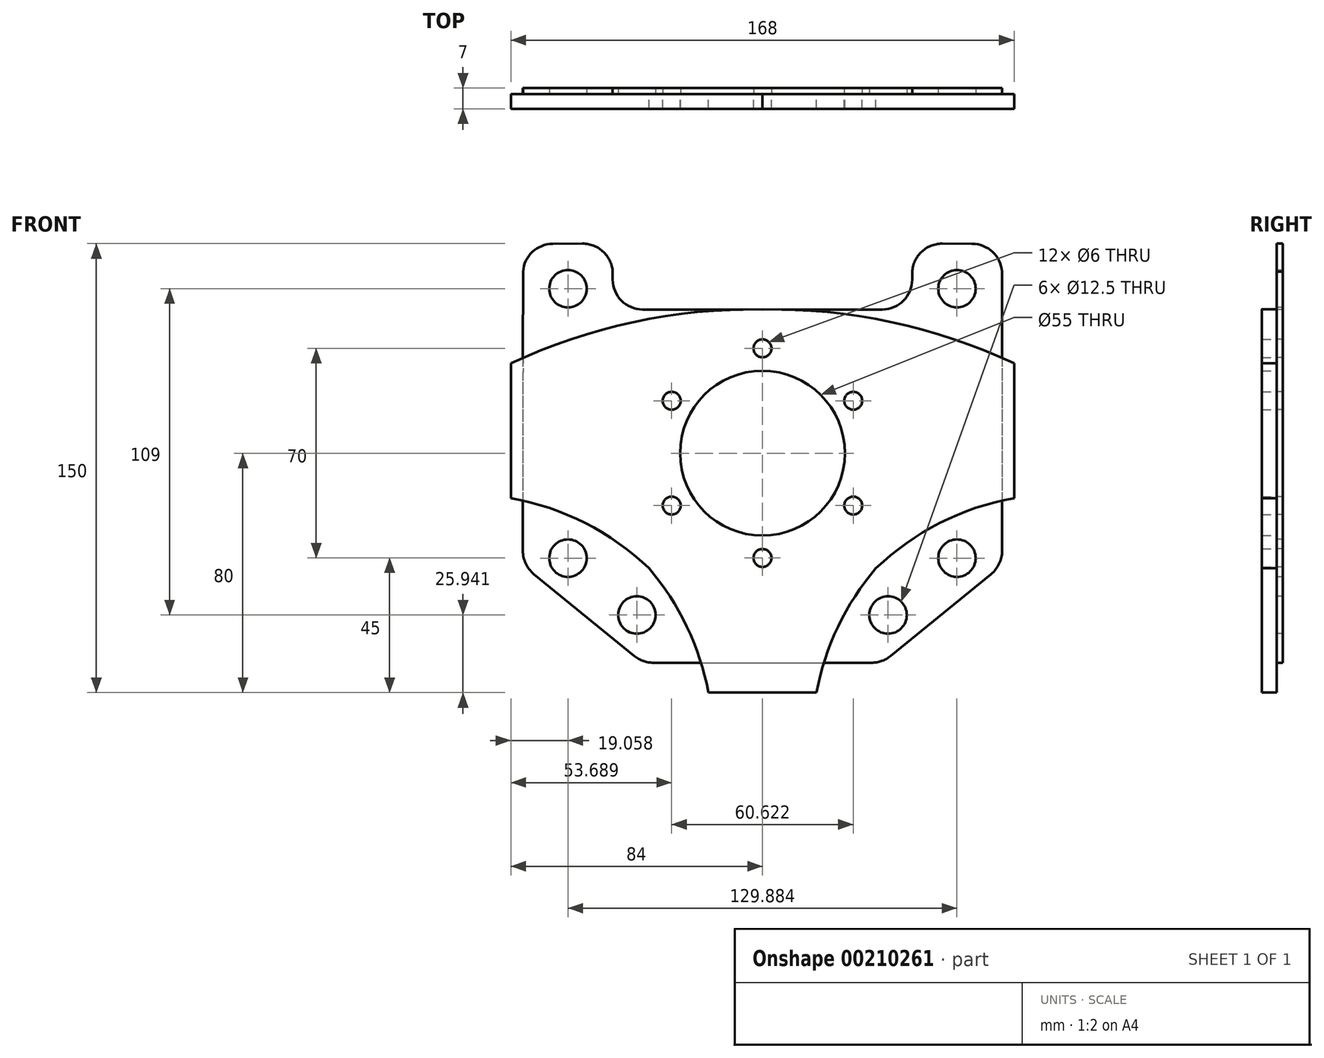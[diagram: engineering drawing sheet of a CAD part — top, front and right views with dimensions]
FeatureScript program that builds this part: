
annotation { "Feature Type Name" : "Feature", "Feature Type Description" : "" }
export const myFeature = defineFeature(function(context is Context, id is Id, definition is map)
    precondition{}
    {
        {
            var Q0;
            Q0=qCreatedBy(makeId("Front.planeOp"),FACE);
            var sketch = newSketch(context, id + "F0", { "sketchPlane" : qUnion([Q0])});
            skCircle(sketch, "E0", {"center": v(0, 0) * mm, "radius": 27.5 * mm});
            skCircle(sketch, "E1", {"center": v(0, 35) * mm, "radius": 3 * mm});
            skCircle(sketch, "E2.1.0", {"center": v(-30.31, 17.5) * mm, "radius": 3 * mm});
            skCircle(sketch, "E2.2.0", {"center": v(-30.31, -17.5) * mm, "radius": 3 * mm});
            skCircle(sketch, "E2.3.0", {"center": v(0, -35) * mm, "radius": 3 * mm});
            skCircle(sketch, "E2.4.0", {"center": v(30.31, -17.5) * mm, "radius": 3 * mm});
            skCircle(sketch, "E2.5.0", {"center": v(30.31, 17.5) * mm, "radius": 3 * mm});
            skLineSegment(sketch, "E3", {"start": v(0, -80) * mm, "end": v(-18, -80) * mm});
            skArc(sketch, "E4", {"start": v(-37.9, -38.47) * mm, "mid": v(-59.22, -23.35) * mm, "end": v(-84, -15) * mm});
            skArc(sketch, "E5", {"start": v(-18, -80) * mm, "mid": v(-25.25, -57.94) * mm, "end": v(-37.9, -38.47) * mm});
            skLineSegment(sketch, "E6", {"start": v(-84, 30) * mm, "end": v(-84, -15) * mm});
            skArc(sketch, "E7", {"start": v(0, 48) * mm, "mid": v(-43.03, 43.8) * mm, "end": v(-84, 30) * mm});
            skArc(sketch, "E8.MirrorCS", {"start": v(0, 48) * mm, "mid": v(43.03, 43.8) * mm, "end": v(84, 30) * mm});
            skLineSegment(sketch, "E9.MirrorCS", {"start": v(84, 30) * mm, "end": v(84, -15) * mm});
            skLineSegment(sketch, "E10.MirrorCS", {"start": v(84, -15) * mm, "end": v(84, -15) * mm});
            skArc(sketch, "E11.MirrorCS", {"start": v(37.9, -38.47) * mm, "mid": v(59.22, -23.35) * mm, "end": v(84, -15) * mm});
            skArc(sketch, "E12.MirrorCS", {"start": v(18, -80) * mm, "mid": v(25.25, -57.94) * mm, "end": v(37.9, -38.47) * mm});
            skLineSegment(sketch, "E13.MirrorCS", {"start": v(0, -80) * mm, "end": v(18, -80) * mm});
            skLineSegment(sketch, "E14", {"start": v(0, 0) * mm, "end": v(37.9, -38.47) * mm});
            skSolve(sketch);
        }
        {
            var Q0;
            Q0=makeQuery(id+"F0.imprint","IMPRINT",FACE,{"disambiguationData":[TD([[makeQuery(id+"F0.imprint","IMPRINT",EDGE,{"derivedFrom":sQuery(id+"F0.wireOp",EDGE,"xvLfkQ3F-fgjy-q9Nn-lcfM-oA4vtxVeLGYN")}),-1.0]])]});
            var Q1;
            {var subQ0=sQuery(id+"F0.wireOp",EDGE,"IXeQJo4f-0NGN-wymH-wL35-tD5XUzaEt9Ii");Q1=makeQuery(id+"F0.imprint","IMPRINT",FACE,{"disambiguationData":[TD([[makeQuery(id+"F0.imprint","IMPRINT",EDGE,{"derivedFrom":subQ0}),-1.0]])]});}
            var Q2;
            Q2=makeQuery(id+"F0.imprint","IMPRINT",FACE,{"disambiguationData":[TD([[makeQuery(id+"F0.imprint","IMPRINT",EDGE,{"derivedFrom":sQuery(id+"F0.wireOp",EDGE,"E0")}),-1.0]])]});
            var Q3;
            {var subQ0=sQuery(id+"F0.wireOp",EDGE,"U97vX6Bn-T6Nm-C19i-UCoZ-bPOguSU8hI4x");Q3=makeQuery(id+"F0.imprint","IMPRINT",FACE,{"disambiguationData":[TD([[makeQuery(id+"F0.imprint","IMPRINT",EDGE,{"derivedFrom":subQ0}),-1.0]])]});}
            var Q4;
            Q4=makeQuery(id+"F0.imprint","IMPRINT",FACE,{"disambiguationData":[TD([[makeQuery(id+"F0.imprint","IMPRINT",EDGE,{"derivedFrom":sQuery(id+"F0.wireOp",EDGE,"iTDH6eJd-3ZuL-mUN2-QFPx-3khqCnK7DwfM")}),-1.0]])]});
            var Q5;
            {var subQ0=sQuery(id+"F0.wireOp",EDGE,"LSPlpz0O-uzcR-zpDg-bx14-Tm5pNzSKurLG");Q5=makeQuery(id+"F0.imprint","IMPRINT",FACE,{"disambiguationData":[TD([[makeQuery(id+"F0.imprint","IMPRINT",EDGE,{"derivedFrom":subQ0}),-1.0]])]});}
            var Q6;
            Q6=makeQuery(id+"F0.imprint","IMPRINT",FACE,{"disambiguationData":[TD([[makeQuery(id+"F0.imprint","IMPRINT",EDGE,{"derivedFrom":sQuery(id+"F0.wireOp",EDGE,"9da5268f-547f-4821-a759-cff2299c6b0c0.MirrorC")}),1.0]])]});
            var Q7;
            Q7=makeQuery(id+"F0.imprint","IMPRINT",FACE,{"disambiguationData":[TD([[makeQuery(id+"F0.imprint","IMPRINT",EDGE,{"derivedFrom":sQuery(id+"F0.wireOp",EDGE,"5ea91802-01c1-4fcd-b629-e54decbf77210.MirrorC")}),1.0]])]});
            extrude(context, id + "F1", {"entities" : qUnion([Q0, Q1, Q2, Q3, Q4, Q5, Q6, Q7]), "depth" : 5 * mm});
        }
        {
            var Q0;
            Q0=qCreatedBy(makeId("Front.planeOp"),FACE);
            var sketch = newSketch(context, id + "F2", { "sketchPlane" : qUnion([Q0])});
            skLineSegment(sketch, "E15", {"start": v(0, 48) * mm, "end": v(-40, 48) * mm});
            skLineSegment(sketch, "E16", {"start": v(-50, 58) * mm, "end": v(-50, 60) * mm});
            skLineSegment(sketch, "E17", {"start": v(-60.06, 70) * mm, "end": v(-70.02, 69.94) * mm});
            skPoint(sketch, "E18.visualSharp", {"position": v(-80.06, 69.88) * mm});
            skArc(sketch, "E18.filletArc", {"start": v(-70.02, 69.94) * mm, "mid": v(-76.81, 67.23) * mm, "end": v(-79.94, 60.62) * mm});
            skPoint(sketch, "E19.visualSharp", {"position": v(-50, 70.06) * mm});
            skArc(sketch, "E19.filletArc", {"start": v(-50, 60) * mm, "mid": v(-52.95, 67.1) * mm, "end": v(-60.06, 70) * mm});
            skPoint(sketch, "E20.visualSharp", {"position": v(-50, 48) * mm});
            skArc(sketch, "E20.filletArc", {"start": v(-50, 58) * mm, "mid": v(-47.07, 50.93) * mm, "end": v(-40, 48) * mm});
            skLineSegment(sketch, "E21", {"start": v(0, 0) * mm, "end": v(0, 35) * mm});
            skCircle(sketch, "E22", {"center": v(0, 35) * mm, "radius": 3 * mm});
            skLineSegment(sketch, "E23", {"start": v(0, 35) * mm, "end": v(0, 48) * mm});
            skLineSegment(sketch, "E24", {"start": v(-42.76, -67.75) * mm, "end": v(-76.32, -40.39) * mm});
            skLineSegment(sketch, "E25", {"start": v(-79.94, 60.62) * mm, "end": v(-80, -32.63) * mm});
            skLineSegment(sketch, "E26", {"start": v(-36.44, -70) * mm, "end": v(0, -70) * mm});
            skPoint(sketch, "E27.visualSharp", {"position": v(-80, -37.38) * mm});
            skArc(sketch, "E27.filletArc", {"start": v(-80, -32.63) * mm, "mid": v(-79.03, -36.92) * mm, "end": v(-76.32, -40.39) * mm});
            skPoint(sketch, "E28.visualSharp", {"position": v(-40, -70) * mm});
            skArc(sketch, "E28.filletArc", {"start": v(-42.76, -67.75) * mm, "mid": v(-39.8, -69.42) * mm, "end": v(-36.44, -70) * mm});
            skCircle(sketch, "E29", {"center": v(-64.94, 54.94) * mm, "radius": 6.25 * mm});
            skCircle(sketch, "E30", {"center": v(-64.94, -35.06) * mm, "radius": 6.25 * mm});
            skCircle(sketch, "E31.1.0", {"center": v(-30.31, 17.5) * mm, "radius": 3 * mm});
            skCircle(sketch, "E31.2.0", {"center": v(-30.31, -17.5) * mm, "radius": 3 * mm});
            skCircle(sketch, "E31.3.0", {"center": v(0, -35) * mm, "radius": 3 * mm});
            skCircle(sketch, "E31.4.0", {"center": v(30.31, -17.5) * mm, "radius": 3 * mm});
            skCircle(sketch, "E31.5.0", {"center": v(30.31, 17.5) * mm, "radius": 3 * mm});
            skPoint(sketch, "E31.center", {"position": v(0, 0) * mm});
            skLineSegment(sketch, "E32.MirrorCS", {"start": v(0, 48) * mm, "end": v(40, 48) * mm});
            skArc(sketch, "E33.MirrorCS", {"start": v(50, 58) * mm, "mid": v(47.07, 50.93) * mm, "end": v(40, 48) * mm});
            skLineSegment(sketch, "E34.MirrorCS", {"start": v(50, 58) * mm, "end": v(50, 60) * mm});
            skArc(sketch, "E35.MirrorCS", {"start": v(50, 60) * mm, "mid": v(52.95, 67.1) * mm, "end": v(60.06, 70) * mm});
            skLineSegment(sketch, "E36.MirrorCS", {"start": v(60.06, 70) * mm, "end": v(70.02, 69.94) * mm});
            skCircle(sketch, "E37.MirrorC", {"center": v(64.94, 54.94) * mm, "radius": 6.25 * mm});
            skArc(sketch, "E38.MirrorCS", {"start": v(70.02, 69.94) * mm, "mid": v(76.81, 67.23) * mm, "end": v(79.94, 60.62) * mm});
            skLineSegment(sketch, "E39.MirrorCS", {"start": v(79.94, 60.62) * mm, "end": v(80, -32.63) * mm});
            skArc(sketch, "E40.MirrorCS", {"start": v(80, -32.63) * mm, "mid": v(79.03, -36.92) * mm, "end": v(76.32, -40.39) * mm});
            skCircle(sketch, "E41.MirrorC", {"center": v(64.94, -35.06) * mm, "radius": 6.25 * mm});
            skLineSegment(sketch, "E42.MirrorCS", {"start": v(42.76, -67.75) * mm, "end": v(76.32, -40.39) * mm});
            skCircle(sketch, "E43.MirrorC", {"center": v(41.94, -54.06) * mm, "radius": 6.25 * mm});
            skLineSegment(sketch, "E44.MirrorCS", {"start": v(36.44, -70) * mm, "end": v(0, -70) * mm});
            skArc(sketch, "E45.MirrorCS", {"start": v(42.76, -67.75) * mm, "mid": v(39.8, -69.42) * mm, "end": v(36.44, -70) * mm});
            skCircle(sketch, "E46.MirrorC", {"center": v(-41.94, -54.06) * mm, "radius": 6.25 * mm});
            skSolve(sketch);
        }
        {
            var Q0;
            Q0=makeQuery(id+"F2.imprint","IMPRINT",FACE,{"disambiguationData":[TD([[makeQuery(id+"F2.imprint","IMPRINT",EDGE,{"derivedFrom":sQuery(id+"F2.wireOp",EDGE,"E15")}),1.0]])]});
            extrude(context, id + "F3", {"entities" : qUnion([Q0]), "oppositeDirection" : true, "depth" : 2 * mm});
        }
    });
